# Revit family: Sanitary_Other_Slits_Toilet-Paper-Holder
name_source: partatom
category: Furniture
units: mm (PartAtom-declared; Revit-internal decimal feet)

## family parameters
Always vertical = No
Cut with Voids When Loaded = No
OmniClass Number = 23.40.20.00
OmniClass Title = General Furniture and Specialties
Room Calculation Point = No
Shared = No
Work Plane-Based = Yes

## types (1)
- Slits spare toilet paper holder
    AssetType = Fixed
    BIMObjectName = Sanitary_Other_Slits_Toilet-Paper-Holder
    Brand = Svedholm
    Color = Various
    Cost = 0 $
    Default Elevation = 1219 mm
    Description = A toilet paper holder made of powder coated steel. All colours are available upon request.
The entire SLITS collection is approved by the Swedish BYGGVARUBEDÖMNINGEN and assessed in SundaHus Material Data.
    DurationUnit = Year
    IfcExportAs = IfcFurnishingElementType
    IfcExportType = MIRROR
    MainColor = White
    Manufacturer = Svedholm
    ManufacturerName = Svedholm
    ManufacturerURL = https://www.svedholm.se
    Material = Metal
    MirrorMainMaterial = RAL 7021
    Model = Slits spare toilet paper holder
    ModelNumber = 410.600.053 for right / 410.600.054  for left
    NBSDescription = Mirrors
    NBSReference = 45-35-72/336
    Name = Slits_Toilet-Paper-Holder
    NominalDepth = 73 mm
    NominalHeight = 68 mm
    NominalLength = 149 mm
    ProductInformation = A toilet paper holder made of powder coated steel. All colours are available upon request.
The entire SLITS collection is approved by the Swedish BYGGVARUBEDÖMNINGEN and assessed in SundaHus Material Data.
    Shape = Sculptured
    Size = 68x149x73 mm
    URL = https://www.svedholm.se
    Uniclass2 = Pr_40_70_22_90
    Uniclass2015Description = Toilet paper dispensers
    Uniclass2015Reference = Pr_40_70_22_90
    Version = 1
    VersionDate = 06/07/2023
    WarrantyDurationUnit = Years

## geometry (parser evidence)
native form markers: Sweep x6
no freeform markers — native parametric forms only
